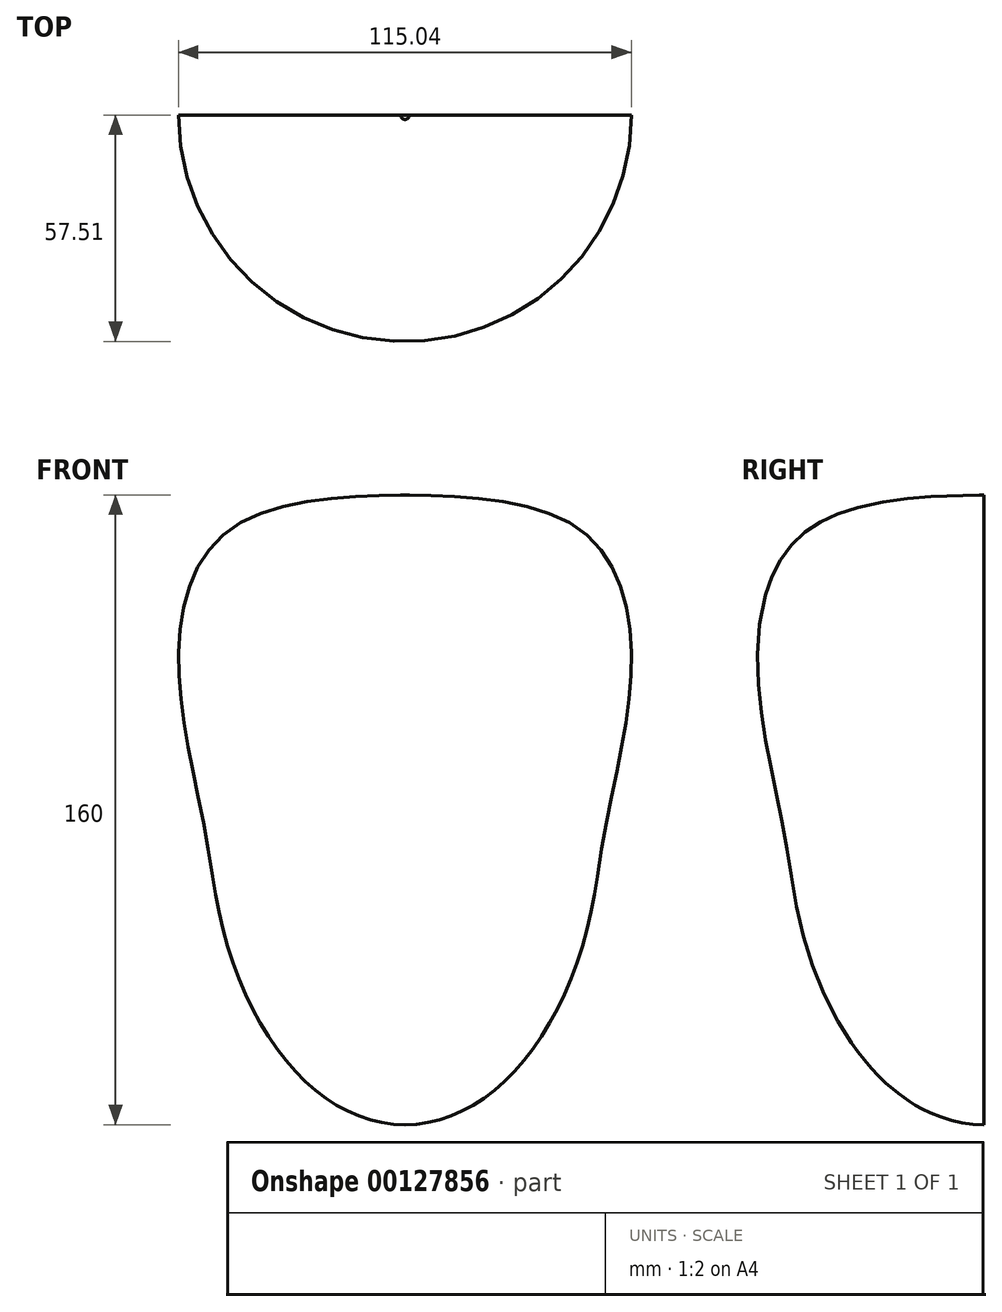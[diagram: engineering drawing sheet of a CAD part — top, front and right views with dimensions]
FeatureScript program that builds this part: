
annotation { "Feature Type Name" : "Feature", "Feature Type Description" : "" }
export const myFeature = defineFeature(function(context is Context, id is Id, definition is map)
    precondition{}
    {
        {
            var Q0;
            Q0=qCreatedBy(makeId("Front.planeOp"),FACE);
            var sketch = newSketch(context, id + "F0", { "sketchPlane" : qUnion([Q0])});
            skEllipticalArc(sketch, "E0", {});
            skLineSegment(sketch, "E1", {"start": v(0, 80) * mm, "end": v(0, -80) * mm});
            skLineSegment(sketch, "E2", {"start": v(0, 0) * mm, "end": v(50, 0) * mm, "construction": true});
            const initialGuessF0  = {"E0": [0, 0, 0, 1, 0.08, 0.05, 3.141592653589793, 0]};
            skSetInitialGuess(sketch, initialGuessF0);
            skSolve(sketch);
        }
        {
            var Q0;
            Q0 = qSketchRegion(id + "F0", true);
            var Q1;
            Q1=sQuery(id+"F0.wireOp",EDGE,"E1");
            revolve(context, id + "F1", {"entities" : qUnion([Q0]), "axis" : qUnion([Q1]), "revolveType" : RevolveType.ONE_DIRECTION, "angle" : 180 * degree});
        }
        {
            var Q0;
            Q0=qCreatedBy(makeId("Front.planeOp"),FACE);
            var sketch = newSketch(context, id + "F2", { "sketchPlane" : qUnion([Q0])});
            skFitSpline(sketch, "E3", {"points": [v(-48.72, -17.96) * mm, v(-57.5, 36.66) * mm, v(-44.26, 71.39) * mm, v(0, 80) * mm], "startDerivative": vector(-22.66, 165.54) * mm, "endDerivative": vector(118.46, 2.08) * mm});
            skPoint(sketch, "E4.orphan", {"position": v(0, -80) * mm});
            skLineSegment(sketch, "E5", {"start": v(0, 80) * mm, "end": v(0, -35.91) * mm, "construction": true});
            skLineSegment(sketch, "E6", {"start": v(57.5, 36.66) * mm, "end": v(-57.5, 36.66) * mm, "construction": true});
            skEllipticalArc(sketch, "E7.1", {});
            skEllipticalArc(sketch, "E8.trimOffspring", {});
            skLineSegment(sketch, "E9.trimOffspring", {"start": v(-48.72, -17.96) * mm, "end": v(-48.72, -17.96) * mm});
            skLineSegment(sketch, "E10", {"start": v(0, -80) * mm, "end": v(0, 80) * mm});
            const initialGuessF2  = {"E7.1": [0, 0, 0, 1, 0.08, 0.05, 0, 0.02217819375512508], "E8.trimOffspring": [0, 0, 0, 1, 0.08, 0.05, 1.7838835639938417, 3.141592653589793]};
            skSetInitialGuess(sketch, initialGuessF2);
            skSolve(sketch);
        }
        {
            var Q0;
            Q0 = qSketchRegion(id + "F2", true);
            var Q1;
            Q1=sQuery(id+"F2.wireOp",EDGE,"E10");
            revolve(context, id + "F3", {"operationType" : NewBodyOperationType.ADD, "entities" : qUnion([Q0]), "axis" : qUnion([Q1]), "revolveType" : RevolveType.ONE_DIRECTION, "angle" : 180 * degree});
        }
    });
